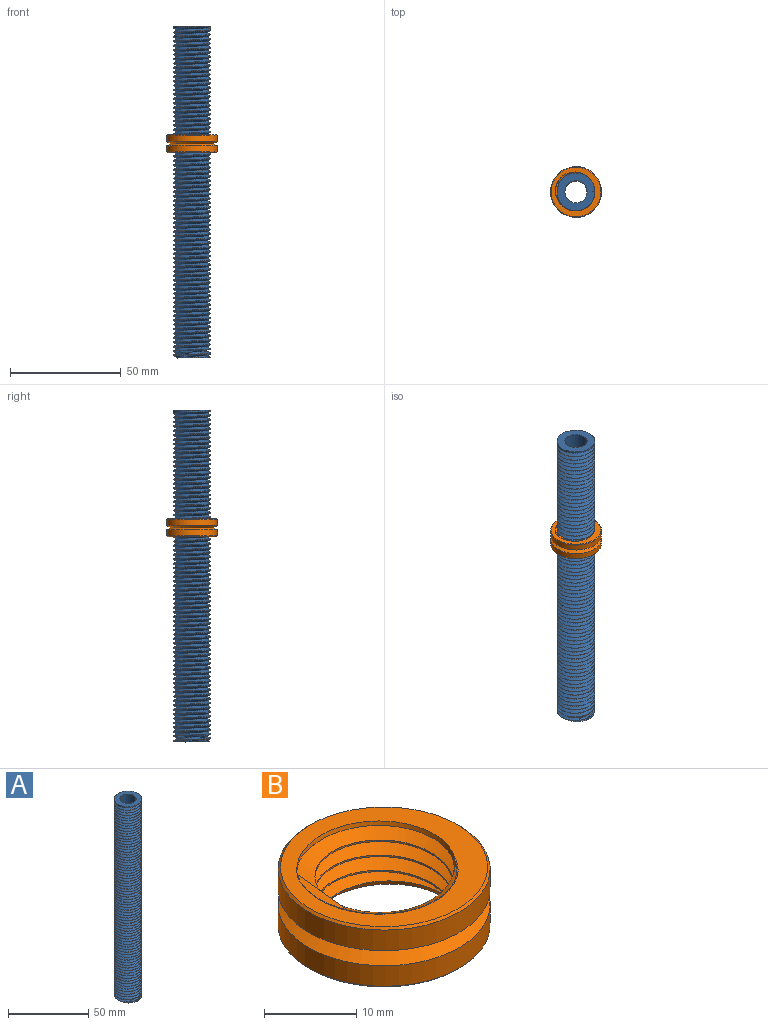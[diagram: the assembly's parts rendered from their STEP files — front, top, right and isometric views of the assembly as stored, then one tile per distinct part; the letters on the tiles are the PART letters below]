
ASSEMBLY  parts=2 mates=1
PART A: 7 faces, bbox 18.2x20.8x152.3 mm
  f0: cylinder r=5mm len=150mm, axis (0,0,-1), area 4712.4mm2, adj f2,f3
  f1: cylinder r=8.5mm len=150mm, axis (0,0,-1), area 2936.3mm2, adj f2,f3,f4,f5,f6
  f2: plane 17x17mm, normal (0,0,1), area 148.4mm2, adj f0,f1
  f3: plane 16.86x16.83mm, normal (0,0,-1), area 113.3mm2, adj f0,f1,f4,f5
  f4: bspline ~150.23x19.63mm, area 6482.2mm2, adj f1,f3,f5,f6
  f5: bspline ~150.9x19.63mm, area 6513.3mm2, adj f1,f3,f4,f6
  f6: plane 1.8x1.56mm, normal (0,-1,0), area 1.4mm2, adj f1,f4,f5
PART B: 15 faces, bbox 23.1x23.1x10.3 mm
  f0: cylinder r=11.5mm len=23mm, axis (0,0,-1), area 197.3mm2, adj f9,f13
  f1: cylinder r=7.5mm len=15mm, axis (0,0,-1), area 32.6mm2, adj f4,f5,f8,f11
  f2: plane 22.52x22.52mm, normal (0,0,1), area 155.7mm2, adj f10,f11,f12
  f3: cylinder r=11.5mm len=23mm, axis (0,0,-1), area 197.3mm2, adj f12,f14
  f4: bspline ~22x19.05mm, area 352.4mm2, adj f1,f5,f8,f10,f11
  f5: bspline ~22x19.05mm, area 351.8mm2, adj f1,f4,f7,f8,f11
  f6: plane 22.52x22.52mm, normal (0,0,-1), area 155.6mm2, adj f7,f8,f9
  f7: bspline ~17.64x14.54mm, area 3.8mm2, adj f5,f6,f8
  f8: bspline ~17.05x11.21mm, area 13.6mm2, adj f1,f4,f5,f6,f7
  f9: cone r=11.5mm half-angle=45deg, axis (0,0,1), area 27.3mm2, adj f0,f6
  f10: bspline ~17.24x14.81mm, area 3.8mm2, adj f2,f4,f11
  f11: bspline ~17.4x16.23mm, area 13.6mm2, adj f1,f2,f4,f5,f10
  f12: cone r=11.23mm half-angle=45deg, axis (0,0,-1), area 27.3mm2, adj f2,f3
  f13: cone r=9.77mm half-angle=60deg, axis (0,0,-1), area 133.6mm2, adj f0,f14
  f14: cone r=11.5mm half-angle=60deg, axis (0,0,1), area 133.6mm2, adj f3,f13
PLACE A t=(-37.91,-6.83,21.95)mm
PLACE B t=(-37.91,-6.83,111.78)mm
MATE slider A.f0 <-> B.f0  axis (0,0,-1) through (-37.91,-6.83,21.95)mm
